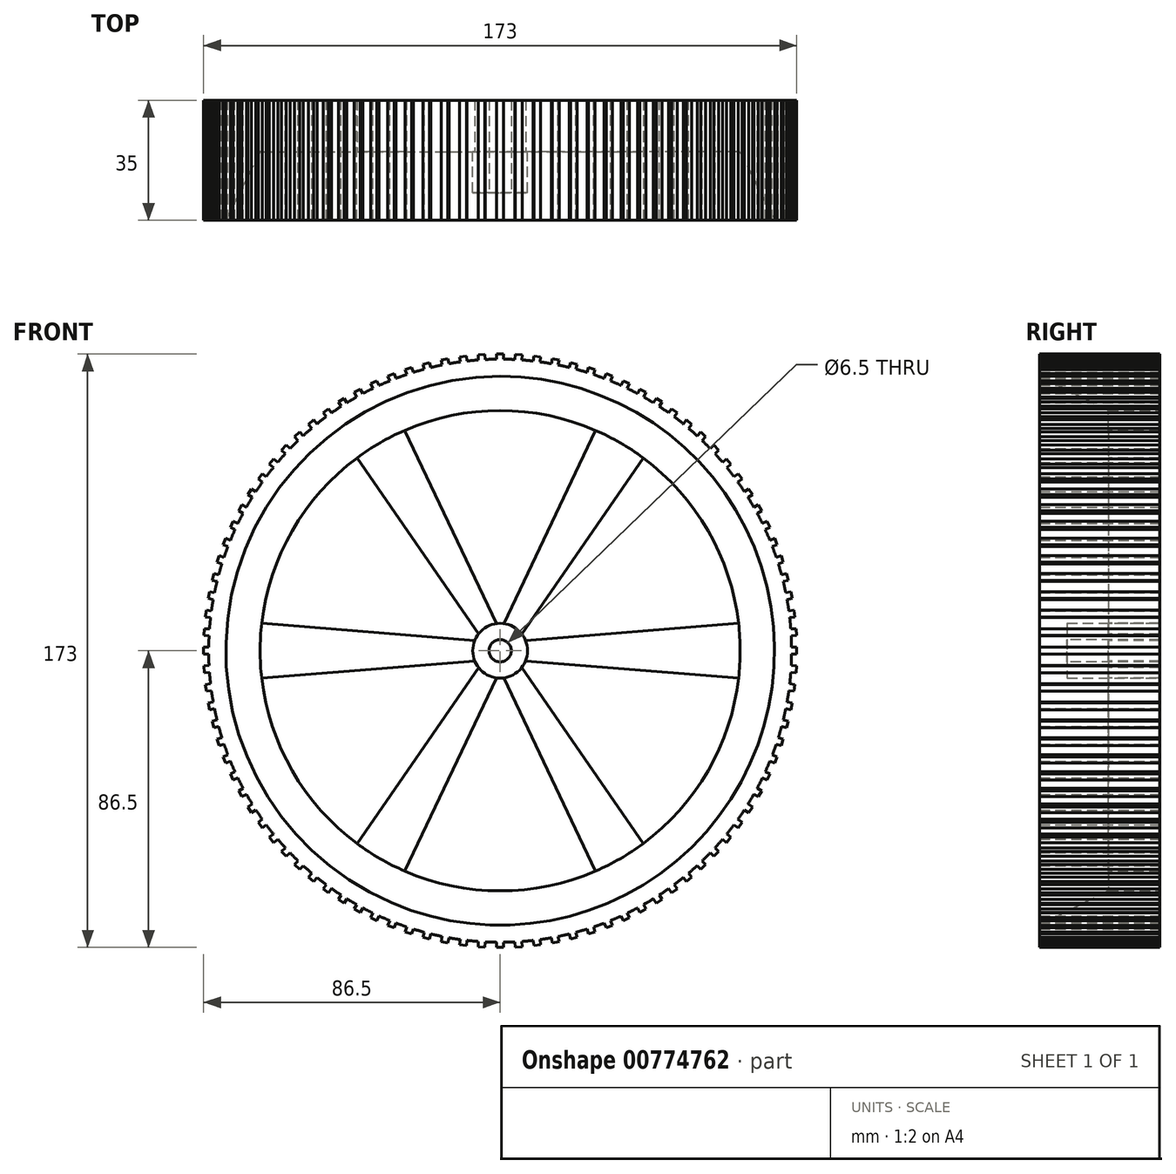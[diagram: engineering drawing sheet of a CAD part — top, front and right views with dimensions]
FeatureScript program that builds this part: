
annotation { "Feature Type Name" : "Feature", "Feature Type Description" : "" }
export const myFeature = defineFeature(function(context is Context, id is Id, definition is map)
    precondition{}
    {
        {
            var Q0;
            Q0=qCreatedBy(makeId("Top.planeOp"),FACE);
            var sketch = newSketch(context, id + "F0", { "sketchPlane" : qUnion([Q0])});
            skLineSegment(sketch, "E0.MirrorCS", {"start": v(-85, -20) * mm, "end": v(-80, -20) * mm});
            skLineSegment(sketch, "E1", {"start": v(-85, 15) * mm, "end": v(0, 15) * mm});
            skLineSegment(sketch, "E2", {"start": v(0, 15) * mm, "end": v(0, 0) * mm});
            skLineSegment(sketch, "E3", {"start": v(-8, 0) * mm, "end": v(-70, 0) * mm});
            skLineSegment(sketch, "E4", {"start": v(-80, -20) * mm, "end": v(-70, 0) * mm});
            skLineSegment(sketch, "E5", {"start": v(-70, 0) * mm, "end": v(-70, 15) * mm});
            skLineSegment(sketch, "E6", {"start": v(-8, 15) * mm, "end": v(-8, 0) * mm});
            skLineSegment(sketch, "E7", {"start": v(-85, 15) * mm, "end": v(-85, -20) * mm});
            skLineSegment(sketch, "E8", {"start": v(0, 0) * mm, "end": v(0, -12) * mm});
            skLineSegment(sketch, "E9", {"start": v(0, -12) * mm, "end": v(-8, -12) * mm});
            skLineSegment(sketch, "E10", {"start": v(-8, -12) * mm, "end": v(-8, 0) * mm});
            skSolve(sketch);
        }
        {
            var Q0;
            Q0=makeQuery(id+"F0.imprint","IMPRINT",FACE,{"disambiguationData":[TD([[makeQuery(id+"F0.imprint","IMPRINT",EDGE,{"derivedFrom":sQuery(id+"F0.wireOp",EDGE,"E0.MirrorCS")}),1.0]])]});
            var Q1;
            {var subQ0=sQuery(id+"F0.wireOp",EDGE,"E2");Q1=makeQuery(id+"F0.imprint","IMPRINT",FACE,{"disambiguationData":[TD([[makeQuery(id+"F0.imprint","IMPRINT",EDGE,{"derivedFrom":subQ0}),-1.0]])]});}
            var Q2;
            Q2=sQuery(id+"F0.wireOp",EDGE,"E2");
            revolve(context, id + "F1", {"surfaceOperationType" : NewSurfaceOperationType.NEW, "entities" : qUnion([Q0, Q1]), "axis" : qUnion([Q2]), "revolveType" : RevolveType.FULL});
        }
        {
            var Q0;
            Q0=qCreatedBy(makeId("Front.planeOp"),FACE);
            var sketch = newSketch(context, id + "F2", { "sketchPlane" : qUnion([Q0])});
            skPoint(sketch, "E11.center", {"position": v(0, 0) * mm});
            skCircle(sketch, "E12.0", {"center": v(0, 0) * mm, "radius": 70 * mm});
            skCircle(sketch, "E13.0", {"center": v(0, 0) * mm, "radius": 8 * mm});
            skLineSegment(sketch, "E14", {"start": v(-69.54, 8) * mm, "end": v(-7.42, 3) * mm});
            skLineSegment(sketch, "E15.MirrorCS", {"start": v(-69.54, -8) * mm, "end": v(-7.42, -3) * mm});
            skLineSegment(sketch, "E16.1.0", {"start": v(-41.7, -56.22) * mm, "end": v(-6.3, -4.92) * mm});
            skLineSegment(sketch, "E16.1.1", {"start": v(-27.84, -64.22) * mm, "end": v(-1.11, -7.92) * mm});
            skLineSegment(sketch, "E16.2.0", {"start": v(27.84, -64.22) * mm, "end": v(1.11, -7.92) * mm});
            skLineSegment(sketch, "E16.2.1", {"start": v(41.7, -56.22) * mm, "end": v(6.3, -4.92) * mm});
            skLineSegment(sketch, "E16.3.0", {"start": v(69.54, -8) * mm, "end": v(7.42, -3) * mm});
            skLineSegment(sketch, "E16.3.1", {"start": v(69.54, 8) * mm, "end": v(7.42, 3) * mm});
            skLineSegment(sketch, "E16.4.0", {"start": v(41.7, 56.22) * mm, "end": v(6.3, 4.92) * mm});
            skLineSegment(sketch, "E16.4.1", {"start": v(27.84, 64.22) * mm, "end": v(1.11, 7.92) * mm});
            skLineSegment(sketch, "E16.5.0", {"start": v(-27.84, 64.22) * mm, "end": v(-1.11, 7.92) * mm});
            skLineSegment(sketch, "E16.5.1", {"start": v(-41.7, 56.22) * mm, "end": v(-6.3, 4.92) * mm});
            skCircle(sketch, "E17.0", {"center": v(0, 0) * mm, "radius": 85 * mm});
            skLineSegment(sketch, "E18", {"start": v(-85, 0) * mm, "end": v(-86.5, 0) * mm, "construction": true});
            skLineSegment(sketch, "E19", {"start": v(-86.5, 1) * mm, "end": v(-86.5, -1) * mm});
            skLineSegment(sketch, "E20", {"start": v(-86.5, 1) * mm, "end": v(-85, 1) * mm});
            skLineSegment(sketch, "E21", {"start": v(-86.5, -1) * mm, "end": v(-85, -1) * mm});
            skLineSegment(sketch, "E22.1.0", {"start": v(-86.27, -6.43) * mm, "end": v(-84.76, -6.33) * mm});
            skLineSegment(sketch, "E22.1.1", {"start": v(-86.4, -4.43) * mm, "end": v(-86.27, -6.43) * mm});
            skLineSegment(sketch, "E22.1.2", {"start": v(-86.4, -4.43) * mm, "end": v(-84.89, -4.34) * mm});
            skLineSegment(sketch, "E22.2.0", {"start": v(-85.7, -11.83) * mm, "end": v(-84.2, -11.64) * mm});
            skLineSegment(sketch, "E22.2.1", {"start": v(-85.94, -9.85) * mm, "end": v(-85.7, -11.83) * mm});
            skLineSegment(sketch, "E22.2.2", {"start": v(-85.94, -9.85) * mm, "end": v(-84.45, -9.66) * mm});
            skLineSegment(sketch, "E22.3.0", {"start": v(-84.78, -17.2) * mm, "end": v(-83.3, -16.9) * mm});
            skLineSegment(sketch, "E22.3.1", {"start": v(-85.16, -15.23) * mm, "end": v(-84.78, -17.2) * mm});
            skLineSegment(sketch, "E22.3.2", {"start": v(-85.16, -15.23) * mm, "end": v(-83.68, -14.94) * mm});
            skLineSegment(sketch, "E22.4.0", {"start": v(-83.53, -22.48) * mm, "end": v(-82.08, -22.1) * mm});
            skLineSegment(sketch, "E22.4.1", {"start": v(-84.03, -20.54) * mm, "end": v(-83.53, -22.48) * mm});
            skLineSegment(sketch, "E22.4.2", {"start": v(-84.03, -20.54) * mm, "end": v(-82.57, -20.17) * mm});
            skLineSegment(sketch, "E22.5.0", {"start": v(-81.96, -27.68) * mm, "end": v(-80.53, -27.22) * mm});
            skLineSegment(sketch, "E22.5.1", {"start": v(-82.58, -25.78) * mm, "end": v(-81.96, -27.68) * mm});
            skLineSegment(sketch, "E22.5.2", {"start": v(-82.58, -25.78) * mm, "end": v(-81.14, -25.31) * mm});
            skLineSegment(sketch, "E22.6.0", {"start": v(-80.06, -32.77) * mm, "end": v(-78.66, -32.22) * mm});
            skLineSegment(sketch, "E22.6.1", {"start": v(-80.8, -30.91) * mm, "end": v(-80.06, -32.77) * mm});
            skLineSegment(sketch, "E22.6.2", {"start": v(-80.8, -30.91) * mm, "end": v(-79.4, -30.36) * mm});
            skLineSegment(sketch, "E22.7.0", {"start": v(-77.84, -37.73) * mm, "end": v(-76.48, -37.1) * mm});
            skLineSegment(sketch, "E22.7.1", {"start": v(-78.7, -35.93) * mm, "end": v(-77.84, -37.73) * mm});
            skLineSegment(sketch, "E22.7.2", {"start": v(-78.7, -35.93) * mm, "end": v(-77.33, -35.28) * mm});
            skLineSegment(sketch, "E22.8.0", {"start": v(-75.32, -42.55) * mm, "end": v(-74, -41.82) * mm});
            skLineSegment(sketch, "E22.8.1", {"start": v(-76.28, -40.8) * mm, "end": v(-75.32, -42.55) * mm});
            skLineSegment(sketch, "E22.8.2", {"start": v(-76.28, -40.8) * mm, "end": v(-74.96, -40.07) * mm});
            skLineSegment(sketch, "E22.9.0", {"start": v(-72.5, -47.2) * mm, "end": v(-71.23, -46.39) * mm});
            skLineSegment(sketch, "E22.9.1", {"start": v(-73.57, -45.5) * mm, "end": v(-72.5, -47.2) * mm});
            skLineSegment(sketch, "E22.9.2", {"start": v(-73.57, -45.5) * mm, "end": v(-72.3, -44.7) * mm});
            skLineSegment(sketch, "E22.10.0", {"start": v(-69.4, -51.65) * mm, "end": v(-68.17, -50.77) * mm});
            skLineSegment(sketch, "E22.10.1", {"start": v(-70.57, -50.03) * mm, "end": v(-69.4, -51.65) * mm});
            skLineSegment(sketch, "E22.10.2", {"start": v(-70.57, -50.03) * mm, "end": v(-69.35, -49.15) * mm});
            skLineSegment(sketch, "E22.11.0", {"start": v(-66.01, -55.9) * mm, "end": v(-64.85, -54.95) * mm});
            skLineSegment(sketch, "E22.11.1", {"start": v(-67.29, -54.37) * mm, "end": v(-66.01, -55.9) * mm});
            skLineSegment(sketch, "E22.11.2", {"start": v(-67.29, -54.37) * mm, "end": v(-66.13, -53.4) * mm});
            skLineSegment(sketch, "E22.12.0", {"start": v(-62.37, -59.94) * mm, "end": v(-61.27, -58.91) * mm});
            skLineSegment(sketch, "E22.12.1", {"start": v(-63.74, -58.48) * mm, "end": v(-62.37, -59.94) * mm});
            skLineSegment(sketch, "E22.12.2", {"start": v(-63.74, -58.48) * mm, "end": v(-62.64, -57.45) * mm});
            skLineSegment(sketch, "E22.13.0", {"start": v(-58.48, -63.74) * mm, "end": v(-57.45, -62.64) * mm});
            skLineSegment(sketch, "E22.13.1", {"start": v(-59.94, -62.37) * mm, "end": v(-58.48, -63.74) * mm});
            skLineSegment(sketch, "E22.13.2", {"start": v(-59.94, -62.37) * mm, "end": v(-58.91, -61.27) * mm});
            skLineSegment(sketch, "E22.14.0", {"start": v(-54.37, -67.29) * mm, "end": v(-53.4, -66.13) * mm});
            skLineSegment(sketch, "E22.14.1", {"start": v(-55.9, -66.01) * mm, "end": v(-54.37, -67.29) * mm});
            skLineSegment(sketch, "E22.14.2", {"start": v(-55.9, -66.01) * mm, "end": v(-54.95, -64.85) * mm});
            skLineSegment(sketch, "E22.15.0", {"start": v(-50.03, -70.57) * mm, "end": v(-49.15, -69.35) * mm});
            skLineSegment(sketch, "E22.15.1", {"start": v(-51.65, -69.4) * mm, "end": v(-50.03, -70.57) * mm});
            skLineSegment(sketch, "E22.15.2", {"start": v(-51.65, -69.4) * mm, "end": v(-50.77, -68.17) * mm});
            skLineSegment(sketch, "E22.16.0", {"start": v(-45.5, -73.57) * mm, "end": v(-44.7, -72.3) * mm});
            skLineSegment(sketch, "E22.16.1", {"start": v(-47.2, -72.5) * mm, "end": v(-45.5, -73.57) * mm});
            skLineSegment(sketch, "E22.16.2", {"start": v(-47.2, -72.5) * mm, "end": v(-46.39, -71.23) * mm});
            skLineSegment(sketch, "E22.17.0", {"start": v(-40.8, -76.28) * mm, "end": v(-40.07, -74.96) * mm});
            skLineSegment(sketch, "E22.17.1", {"start": v(-42.55, -75.32) * mm, "end": v(-40.8, -76.28) * mm});
            skLineSegment(sketch, "E22.17.2", {"start": v(-42.55, -75.32) * mm, "end": v(-41.82, -74) * mm});
            skLineSegment(sketch, "E22.18.0", {"start": v(-35.93, -78.7) * mm, "end": v(-35.28, -77.33) * mm});
            skLineSegment(sketch, "E22.18.1", {"start": v(-37.73, -77.84) * mm, "end": v(-35.93, -78.7) * mm});
            skLineSegment(sketch, "E22.18.2", {"start": v(-37.73, -77.84) * mm, "end": v(-37.1, -76.48) * mm});
            skLineSegment(sketch, "E22.19.0", {"start": v(-30.91, -80.8) * mm, "end": v(-30.36, -79.4) * mm});
            skLineSegment(sketch, "E22.19.1", {"start": v(-32.77, -80.06) * mm, "end": v(-30.91, -80.8) * mm});
            skLineSegment(sketch, "E22.19.2", {"start": v(-32.77, -80.06) * mm, "end": v(-32.22, -78.66) * mm});
            skLineSegment(sketch, "E22.20.0", {"start": v(-25.78, -82.58) * mm, "end": v(-25.31, -81.14) * mm});
            skLineSegment(sketch, "E22.20.1", {"start": v(-27.68, -81.96) * mm, "end": v(-25.78, -82.58) * mm});
            skLineSegment(sketch, "E22.20.2", {"start": v(-27.68, -81.96) * mm, "end": v(-27.22, -80.53) * mm});
            skLineSegment(sketch, "E22.21.0", {"start": v(-20.54, -84.03) * mm, "end": v(-20.17, -82.57) * mm});
            skLineSegment(sketch, "E22.21.1", {"start": v(-22.48, -83.53) * mm, "end": v(-20.54, -84.03) * mm});
            skLineSegment(sketch, "E22.21.2", {"start": v(-22.48, -83.53) * mm, "end": v(-22.1, -82.08) * mm});
            skLineSegment(sketch, "E22.22.0", {"start": v(-15.23, -85.16) * mm, "end": v(-14.94, -83.68) * mm});
            skLineSegment(sketch, "E22.22.1", {"start": v(-17.2, -84.78) * mm, "end": v(-15.23, -85.16) * mm});
            skLineSegment(sketch, "E22.22.2", {"start": v(-17.2, -84.78) * mm, "end": v(-16.9, -83.3) * mm});
            skLineSegment(sketch, "E22.23.0", {"start": v(-9.85, -85.94) * mm, "end": v(-9.66, -84.45) * mm});
            skLineSegment(sketch, "E22.23.1", {"start": v(-11.83, -85.7) * mm, "end": v(-9.85, -85.94) * mm});
            skLineSegment(sketch, "E22.23.2", {"start": v(-11.83, -85.7) * mm, "end": v(-11.64, -84.2) * mm});
            skLineSegment(sketch, "E22.24.0", {"start": v(-4.43, -86.4) * mm, "end": v(-4.34, -84.89) * mm});
            skLineSegment(sketch, "E22.24.1", {"start": v(-6.43, -86.27) * mm, "end": v(-4.43, -86.4) * mm});
            skLineSegment(sketch, "E22.24.2", {"start": v(-6.43, -86.27) * mm, "end": v(-6.33, -84.76) * mm});
            skLineSegment(sketch, "E22.25.0", {"start": v(1, -86.5) * mm, "end": v(1, -85) * mm});
            skLineSegment(sketch, "E22.25.1", {"start": v(-1, -86.5) * mm, "end": v(1, -86.5) * mm});
            skLineSegment(sketch, "E22.25.2", {"start": v(-1, -86.5) * mm, "end": v(-1, -85) * mm});
            skLineSegment(sketch, "E22.26.0", {"start": v(6.43, -86.27) * mm, "end": v(6.33, -84.76) * mm});
            skLineSegment(sketch, "E22.26.1", {"start": v(4.43, -86.4) * mm, "end": v(6.43, -86.27) * mm});
            skLineSegment(sketch, "E22.26.2", {"start": v(4.43, -86.4) * mm, "end": v(4.34, -84.89) * mm});
            skLineSegment(sketch, "E22.27.0", {"start": v(11.83, -85.7) * mm, "end": v(11.64, -84.2) * mm});
            skLineSegment(sketch, "E22.27.1", {"start": v(9.85, -85.94) * mm, "end": v(11.83, -85.7) * mm});
            skLineSegment(sketch, "E22.27.2", {"start": v(9.85, -85.94) * mm, "end": v(9.66, -84.45) * mm});
            skLineSegment(sketch, "E22.28.0", {"start": v(17.2, -84.78) * mm, "end": v(16.9, -83.3) * mm});
            skLineSegment(sketch, "E22.28.1", {"start": v(15.23, -85.16) * mm, "end": v(17.2, -84.78) * mm});
            skLineSegment(sketch, "E22.28.2", {"start": v(15.23, -85.16) * mm, "end": v(14.94, -83.68) * mm});
            skLineSegment(sketch, "E22.29.0", {"start": v(22.48, -83.53) * mm, "end": v(22.1, -82.08) * mm});
            skLineSegment(sketch, "E22.29.1", {"start": v(20.54, -84.03) * mm, "end": v(22.48, -83.53) * mm});
            skLineSegment(sketch, "E22.29.2", {"start": v(20.54, -84.03) * mm, "end": v(20.17, -82.57) * mm});
            skLineSegment(sketch, "E22.30.0", {"start": v(27.68, -81.96) * mm, "end": v(27.22, -80.53) * mm});
            skLineSegment(sketch, "E22.30.1", {"start": v(25.78, -82.58) * mm, "end": v(27.68, -81.96) * mm});
            skLineSegment(sketch, "E22.30.2", {"start": v(25.78, -82.58) * mm, "end": v(25.31, -81.14) * mm});
            skLineSegment(sketch, "E22.31.0", {"start": v(32.77, -80.06) * mm, "end": v(32.22, -78.66) * mm});
            skLineSegment(sketch, "E22.31.1", {"start": v(30.91, -80.8) * mm, "end": v(32.77, -80.06) * mm});
            skLineSegment(sketch, "E22.31.2", {"start": v(30.91, -80.8) * mm, "end": v(30.36, -79.4) * mm});
            skLineSegment(sketch, "E22.32.0", {"start": v(37.73, -77.84) * mm, "end": v(37.1, -76.48) * mm});
            skLineSegment(sketch, "E22.32.1", {"start": v(35.93, -78.7) * mm, "end": v(37.73, -77.84) * mm});
            skLineSegment(sketch, "E22.32.2", {"start": v(35.93, -78.7) * mm, "end": v(35.28, -77.33) * mm});
            skLineSegment(sketch, "E22.33.0", {"start": v(42.55, -75.32) * mm, "end": v(41.82, -74) * mm});
            skLineSegment(sketch, "E22.33.1", {"start": v(40.8, -76.28) * mm, "end": v(42.55, -75.32) * mm});
            skLineSegment(sketch, "E22.33.2", {"start": v(40.8, -76.28) * mm, "end": v(40.07, -74.96) * mm});
            skLineSegment(sketch, "E22.34.0", {"start": v(47.2, -72.5) * mm, "end": v(46.39, -71.23) * mm});
            skLineSegment(sketch, "E22.34.1", {"start": v(45.5, -73.57) * mm, "end": v(47.2, -72.5) * mm});
            skLineSegment(sketch, "E22.34.2", {"start": v(45.5, -73.57) * mm, "end": v(44.7, -72.3) * mm});
            skLineSegment(sketch, "E22.35.0", {"start": v(51.65, -69.4) * mm, "end": v(50.77, -68.17) * mm});
            skLineSegment(sketch, "E22.35.1", {"start": v(50.03, -70.57) * mm, "end": v(51.65, -69.4) * mm});
            skLineSegment(sketch, "E22.35.2", {"start": v(50.03, -70.57) * mm, "end": v(49.15, -69.35) * mm});
            skLineSegment(sketch, "E22.36.0", {"start": v(55.9, -66.01) * mm, "end": v(54.95, -64.85) * mm});
            skLineSegment(sketch, "E22.36.1", {"start": v(54.37, -67.29) * mm, "end": v(55.9, -66.01) * mm});
            skLineSegment(sketch, "E22.36.2", {"start": v(54.37, -67.29) * mm, "end": v(53.4, -66.13) * mm});
            skLineSegment(sketch, "E22.37.0", {"start": v(59.94, -62.37) * mm, "end": v(58.91, -61.27) * mm});
            skLineSegment(sketch, "E22.37.1", {"start": v(58.48, -63.74) * mm, "end": v(59.94, -62.37) * mm});
            skLineSegment(sketch, "E22.37.2", {"start": v(58.48, -63.74) * mm, "end": v(57.45, -62.64) * mm});
            skLineSegment(sketch, "E22.38.0", {"start": v(63.74, -58.48) * mm, "end": v(62.64, -57.45) * mm});
            skLineSegment(sketch, "E22.38.1", {"start": v(62.37, -59.94) * mm, "end": v(63.74, -58.48) * mm});
            skLineSegment(sketch, "E22.38.2", {"start": v(62.37, -59.94) * mm, "end": v(61.27, -58.91) * mm});
            skLineSegment(sketch, "E22.39.0", {"start": v(67.29, -54.37) * mm, "end": v(66.13, -53.4) * mm});
            skLineSegment(sketch, "E22.39.1", {"start": v(66.01, -55.9) * mm, "end": v(67.29, -54.37) * mm});
            skLineSegment(sketch, "E22.39.2", {"start": v(66.01, -55.9) * mm, "end": v(64.85, -54.95) * mm});
            skLineSegment(sketch, "E22.40.0", {"start": v(70.57, -50.03) * mm, "end": v(69.35, -49.15) * mm});
            skLineSegment(sketch, "E22.40.1", {"start": v(69.4, -51.65) * mm, "end": v(70.57, -50.03) * mm});
            skLineSegment(sketch, "E22.40.2", {"start": v(69.4, -51.65) * mm, "end": v(68.17, -50.77) * mm});
            skLineSegment(sketch, "E22.41.0", {"start": v(73.57, -45.5) * mm, "end": v(72.3, -44.7) * mm});
            skLineSegment(sketch, "E22.41.1", {"start": v(72.5, -47.2) * mm, "end": v(73.57, -45.5) * mm});
            skLineSegment(sketch, "E22.41.2", {"start": v(72.5, -47.2) * mm, "end": v(71.23, -46.39) * mm});
            skLineSegment(sketch, "E22.42.0", {"start": v(76.28, -40.8) * mm, "end": v(74.96, -40.07) * mm});
            skLineSegment(sketch, "E22.42.1", {"start": v(75.32, -42.55) * mm, "end": v(76.28, -40.8) * mm});
            skLineSegment(sketch, "E22.42.2", {"start": v(75.32, -42.55) * mm, "end": v(74, -41.82) * mm});
            skLineSegment(sketch, "E22.43.0", {"start": v(78.7, -35.93) * mm, "end": v(77.33, -35.28) * mm});
            skLineSegment(sketch, "E22.43.1", {"start": v(77.84, -37.73) * mm, "end": v(78.7, -35.93) * mm});
            skLineSegment(sketch, "E22.43.2", {"start": v(77.84, -37.73) * mm, "end": v(76.48, -37.1) * mm});
            skLineSegment(sketch, "E22.44.0", {"start": v(80.8, -30.91) * mm, "end": v(79.4, -30.36) * mm});
            skLineSegment(sketch, "E22.44.1", {"start": v(80.06, -32.77) * mm, "end": v(80.8, -30.91) * mm});
            skLineSegment(sketch, "E22.44.2", {"start": v(80.06, -32.77) * mm, "end": v(78.66, -32.22) * mm});
            skLineSegment(sketch, "E22.45.0", {"start": v(82.58, -25.78) * mm, "end": v(81.14, -25.31) * mm});
            skLineSegment(sketch, "E22.45.1", {"start": v(81.96, -27.68) * mm, "end": v(82.58, -25.78) * mm});
            skLineSegment(sketch, "E22.45.2", {"start": v(81.96, -27.68) * mm, "end": v(80.53, -27.22) * mm});
            skLineSegment(sketch, "E22.46.0", {"start": v(84.03, -20.54) * mm, "end": v(82.57, -20.17) * mm});
            skLineSegment(sketch, "E22.46.1", {"start": v(83.53, -22.48) * mm, "end": v(84.03, -20.54) * mm});
            skLineSegment(sketch, "E22.46.2", {"start": v(83.53, -22.48) * mm, "end": v(82.08, -22.1) * mm});
            skLineSegment(sketch, "E22.47.0", {"start": v(85.16, -15.23) * mm, "end": v(83.68, -14.94) * mm});
            skLineSegment(sketch, "E22.47.1", {"start": v(84.78, -17.2) * mm, "end": v(85.16, -15.23) * mm});
            skLineSegment(sketch, "E22.47.2", {"start": v(84.78, -17.2) * mm, "end": v(83.3, -16.9) * mm});
            skLineSegment(sketch, "E22.48.0", {"start": v(85.94, -9.85) * mm, "end": v(84.45, -9.66) * mm});
            skLineSegment(sketch, "E22.48.1", {"start": v(85.7, -11.83) * mm, "end": v(85.94, -9.85) * mm});
            skLineSegment(sketch, "E22.48.2", {"start": v(85.7, -11.83) * mm, "end": v(84.2, -11.64) * mm});
            skLineSegment(sketch, "E22.49.0", {"start": v(86.4, -4.43) * mm, "end": v(84.89, -4.34) * mm});
            skLineSegment(sketch, "E22.49.1", {"start": v(86.27, -6.43) * mm, "end": v(86.4, -4.43) * mm});
            skLineSegment(sketch, "E22.49.2", {"start": v(86.27, -6.43) * mm, "end": v(84.76, -6.33) * mm});
            skLineSegment(sketch, "E22.50.0", {"start": v(86.5, 1) * mm, "end": v(85, 1) * mm});
            skLineSegment(sketch, "E22.50.1", {"start": v(86.5, -1) * mm, "end": v(86.5, 1) * mm});
            skLineSegment(sketch, "E22.50.2", {"start": v(86.5, -1) * mm, "end": v(85, -1) * mm});
            skLineSegment(sketch, "E22.51.0", {"start": v(86.27, 6.43) * mm, "end": v(84.76, 6.33) * mm});
            skLineSegment(sketch, "E22.51.1", {"start": v(86.4, 4.43) * mm, "end": v(86.27, 6.43) * mm});
            skLineSegment(sketch, "E22.51.2", {"start": v(86.4, 4.43) * mm, "end": v(84.89, 4.34) * mm});
            skLineSegment(sketch, "E22.52.0", {"start": v(85.7, 11.83) * mm, "end": v(84.2, 11.64) * mm});
            skLineSegment(sketch, "E22.52.1", {"start": v(85.94, 9.85) * mm, "end": v(85.7, 11.83) * mm});
            skLineSegment(sketch, "E22.52.2", {"start": v(85.94, 9.85) * mm, "end": v(84.45, 9.66) * mm});
            skLineSegment(sketch, "E22.53.0", {"start": v(84.78, 17.2) * mm, "end": v(83.3, 16.9) * mm});
            skLineSegment(sketch, "E22.53.1", {"start": v(85.16, 15.23) * mm, "end": v(84.78, 17.2) * mm});
            skLineSegment(sketch, "E22.53.2", {"start": v(85.16, 15.23) * mm, "end": v(83.68, 14.94) * mm});
            skLineSegment(sketch, "E22.54.0", {"start": v(83.53, 22.48) * mm, "end": v(82.08, 22.1) * mm});
            skLineSegment(sketch, "E22.54.1", {"start": v(84.03, 20.54) * mm, "end": v(83.53, 22.48) * mm});
            skLineSegment(sketch, "E22.54.2", {"start": v(84.03, 20.54) * mm, "end": v(82.57, 20.17) * mm});
            skLineSegment(sketch, "E22.55.0", {"start": v(81.96, 27.68) * mm, "end": v(80.53, 27.22) * mm});
            skLineSegment(sketch, "E22.55.1", {"start": v(82.58, 25.78) * mm, "end": v(81.96, 27.68) * mm});
            skLineSegment(sketch, "E22.55.2", {"start": v(82.58, 25.78) * mm, "end": v(81.14, 25.31) * mm});
            skLineSegment(sketch, "E22.56.0", {"start": v(80.06, 32.77) * mm, "end": v(78.66, 32.22) * mm});
            skLineSegment(sketch, "E22.56.1", {"start": v(80.8, 30.91) * mm, "end": v(80.06, 32.77) * mm});
            skLineSegment(sketch, "E22.56.2", {"start": v(80.8, 30.91) * mm, "end": v(79.4, 30.36) * mm});
            skLineSegment(sketch, "E22.57.0", {"start": v(77.84, 37.73) * mm, "end": v(76.48, 37.1) * mm});
            skLineSegment(sketch, "E22.57.1", {"start": v(78.7, 35.93) * mm, "end": v(77.84, 37.73) * mm});
            skLineSegment(sketch, "E22.57.2", {"start": v(78.7, 35.93) * mm, "end": v(77.33, 35.28) * mm});
            skLineSegment(sketch, "E22.58.0", {"start": v(75.32, 42.55) * mm, "end": v(74, 41.82) * mm});
            skLineSegment(sketch, "E22.58.1", {"start": v(76.28, 40.8) * mm, "end": v(75.32, 42.55) * mm});
            skLineSegment(sketch, "E22.58.2", {"start": v(76.28, 40.8) * mm, "end": v(74.96, 40.07) * mm});
            skLineSegment(sketch, "E22.59.0", {"start": v(72.5, 47.2) * mm, "end": v(71.23, 46.39) * mm});
            skLineSegment(sketch, "E22.59.1", {"start": v(73.57, 45.5) * mm, "end": v(72.5, 47.2) * mm});
            skLineSegment(sketch, "E22.59.2", {"start": v(73.57, 45.5) * mm, "end": v(72.3, 44.7) * mm});
            skLineSegment(sketch, "E22.60.0", {"start": v(69.4, 51.65) * mm, "end": v(68.17, 50.77) * mm});
            skLineSegment(sketch, "E22.60.1", {"start": v(70.57, 50.03) * mm, "end": v(69.4, 51.65) * mm});
            skLineSegment(sketch, "E22.60.2", {"start": v(70.57, 50.03) * mm, "end": v(69.35, 49.15) * mm});
            skLineSegment(sketch, "E22.61.0", {"start": v(66.01, 55.9) * mm, "end": v(64.85, 54.95) * mm});
            skLineSegment(sketch, "E22.61.1", {"start": v(67.29, 54.37) * mm, "end": v(66.01, 55.9) * mm});
            skLineSegment(sketch, "E22.61.2", {"start": v(67.29, 54.37) * mm, "end": v(66.13, 53.4) * mm});
            skLineSegment(sketch, "E22.62.0", {"start": v(62.37, 59.94) * mm, "end": v(61.27, 58.91) * mm});
            skLineSegment(sketch, "E22.62.1", {"start": v(63.74, 58.48) * mm, "end": v(62.37, 59.94) * mm});
            skLineSegment(sketch, "E22.62.2", {"start": v(63.74, 58.48) * mm, "end": v(62.64, 57.45) * mm});
            skLineSegment(sketch, "E22.63.0", {"start": v(58.48, 63.74) * mm, "end": v(57.45, 62.64) * mm});
            skLineSegment(sketch, "E22.63.1", {"start": v(59.94, 62.37) * mm, "end": v(58.48, 63.74) * mm});
            skLineSegment(sketch, "E22.63.2", {"start": v(59.94, 62.37) * mm, "end": v(58.91, 61.27) * mm});
            skLineSegment(sketch, "E22.64.0", {"start": v(54.37, 67.29) * mm, "end": v(53.4, 66.13) * mm});
            skLineSegment(sketch, "E22.64.1", {"start": v(55.9, 66.01) * mm, "end": v(54.37, 67.29) * mm});
            skLineSegment(sketch, "E22.64.2", {"start": v(55.9, 66.01) * mm, "end": v(54.95, 64.85) * mm});
            skLineSegment(sketch, "E22.65.0", {"start": v(50.03, 70.57) * mm, "end": v(49.15, 69.35) * mm});
            skLineSegment(sketch, "E22.65.1", {"start": v(51.65, 69.4) * mm, "end": v(50.03, 70.57) * mm});
            skLineSegment(sketch, "E22.65.2", {"start": v(51.65, 69.4) * mm, "end": v(50.77, 68.17) * mm});
            skLineSegment(sketch, "E22.66.0", {"start": v(45.5, 73.57) * mm, "end": v(44.7, 72.3) * mm});
            skLineSegment(sketch, "E22.66.1", {"start": v(47.2, 72.5) * mm, "end": v(45.5, 73.57) * mm});
            skLineSegment(sketch, "E22.66.2", {"start": v(47.2, 72.5) * mm, "end": v(46.39, 71.23) * mm});
            skLineSegment(sketch, "E22.67.0", {"start": v(40.8, 76.28) * mm, "end": v(40.07, 74.96) * mm});
            skLineSegment(sketch, "E22.67.1", {"start": v(42.55, 75.32) * mm, "end": v(40.8, 76.28) * mm});
            skLineSegment(sketch, "E22.67.2", {"start": v(42.55, 75.32) * mm, "end": v(41.82, 74) * mm});
            skLineSegment(sketch, "E22.68.0", {"start": v(35.93, 78.7) * mm, "end": v(35.28, 77.33) * mm});
            skLineSegment(sketch, "E22.68.1", {"start": v(37.73, 77.84) * mm, "end": v(35.93, 78.7) * mm});
            skLineSegment(sketch, "E22.68.2", {"start": v(37.73, 77.84) * mm, "end": v(37.1, 76.48) * mm});
            skLineSegment(sketch, "E22.69.0", {"start": v(30.91, 80.8) * mm, "end": v(30.36, 79.4) * mm});
            skLineSegment(sketch, "E22.69.1", {"start": v(32.77, 80.06) * mm, "end": v(30.91, 80.8) * mm});
            skLineSegment(sketch, "E22.69.2", {"start": v(32.77, 80.06) * mm, "end": v(32.22, 78.66) * mm});
            skLineSegment(sketch, "E22.70.0", {"start": v(25.78, 82.58) * mm, "end": v(25.31, 81.14) * mm});
            skLineSegment(sketch, "E22.70.1", {"start": v(27.68, 81.96) * mm, "end": v(25.78, 82.58) * mm});
            skLineSegment(sketch, "E22.70.2", {"start": v(27.68, 81.96) * mm, "end": v(27.22, 80.53) * mm});
            skLineSegment(sketch, "E22.71.0", {"start": v(20.54, 84.03) * mm, "end": v(20.17, 82.57) * mm});
            skLineSegment(sketch, "E22.71.1", {"start": v(22.48, 83.53) * mm, "end": v(20.54, 84.03) * mm});
            skLineSegment(sketch, "E22.71.2", {"start": v(22.48, 83.53) * mm, "end": v(22.1, 82.08) * mm});
            skLineSegment(sketch, "E22.72.0", {"start": v(15.23, 85.16) * mm, "end": v(14.94, 83.68) * mm});
            skLineSegment(sketch, "E22.72.1", {"start": v(17.2, 84.78) * mm, "end": v(15.23, 85.16) * mm});
            skLineSegment(sketch, "E22.72.2", {"start": v(17.2, 84.78) * mm, "end": v(16.9, 83.3) * mm});
            skLineSegment(sketch, "E22.73.0", {"start": v(9.85, 85.94) * mm, "end": v(9.66, 84.45) * mm});
            skLineSegment(sketch, "E22.73.1", {"start": v(11.83, 85.7) * mm, "end": v(9.85, 85.94) * mm});
            skLineSegment(sketch, "E22.73.2", {"start": v(11.83, 85.7) * mm, "end": v(11.64, 84.2) * mm});
            skLineSegment(sketch, "E22.74.0", {"start": v(4.43, 86.4) * mm, "end": v(4.34, 84.89) * mm});
            skLineSegment(sketch, "E22.74.1", {"start": v(6.43, 86.27) * mm, "end": v(4.43, 86.4) * mm});
            skLineSegment(sketch, "E22.74.2", {"start": v(6.43, 86.27) * mm, "end": v(6.33, 84.76) * mm});
            skLineSegment(sketch, "E22.75.0", {"start": v(-1, 86.5) * mm, "end": v(-1, 85) * mm});
            skLineSegment(sketch, "E22.75.1", {"start": v(1, 86.5) * mm, "end": v(-1, 86.5) * mm});
            skLineSegment(sketch, "E22.75.2", {"start": v(1, 86.5) * mm, "end": v(1, 85) * mm});
            skLineSegment(sketch, "E22.76.0", {"start": v(-6.43, 86.27) * mm, "end": v(-6.33, 84.76) * mm});
            skLineSegment(sketch, "E22.76.1", {"start": v(-4.43, 86.4) * mm, "end": v(-6.43, 86.27) * mm});
            skLineSegment(sketch, "E22.76.2", {"start": v(-4.43, 86.4) * mm, "end": v(-4.34, 84.89) * mm});
            skLineSegment(sketch, "E22.77.0", {"start": v(-11.83, 85.7) * mm, "end": v(-11.64, 84.2) * mm});
            skLineSegment(sketch, "E22.77.1", {"start": v(-9.85, 85.94) * mm, "end": v(-11.83, 85.7) * mm});
            skLineSegment(sketch, "E22.77.2", {"start": v(-9.85, 85.94) * mm, "end": v(-9.66, 84.45) * mm});
            skLineSegment(sketch, "E22.78.0", {"start": v(-17.2, 84.78) * mm, "end": v(-16.9, 83.3) * mm});
            skLineSegment(sketch, "E22.78.1", {"start": v(-15.23, 85.16) * mm, "end": v(-17.2, 84.78) * mm});
            skLineSegment(sketch, "E22.78.2", {"start": v(-15.23, 85.16) * mm, "end": v(-14.94, 83.68) * mm});
            skLineSegment(sketch, "E22.79.0", {"start": v(-22.48, 83.53) * mm, "end": v(-22.1, 82.08) * mm});
            skLineSegment(sketch, "E22.79.1", {"start": v(-20.54, 84.03) * mm, "end": v(-22.48, 83.53) * mm});
            skLineSegment(sketch, "E22.79.2", {"start": v(-20.54, 84.03) * mm, "end": v(-20.17, 82.57) * mm});
            skLineSegment(sketch, "E22.80.0", {"start": v(-27.68, 81.96) * mm, "end": v(-27.22, 80.53) * mm});
            skLineSegment(sketch, "E22.80.1", {"start": v(-25.78, 82.58) * mm, "end": v(-27.68, 81.96) * mm});
            skLineSegment(sketch, "E22.80.2", {"start": v(-25.78, 82.58) * mm, "end": v(-25.31, 81.14) * mm});
            skLineSegment(sketch, "E22.81.0", {"start": v(-32.77, 80.06) * mm, "end": v(-32.22, 78.66) * mm});
            skLineSegment(sketch, "E22.81.1", {"start": v(-30.91, 80.8) * mm, "end": v(-32.77, 80.06) * mm});
            skLineSegment(sketch, "E22.81.2", {"start": v(-30.91, 80.8) * mm, "end": v(-30.36, 79.4) * mm});
            skLineSegment(sketch, "E22.82.0", {"start": v(-37.73, 77.84) * mm, "end": v(-37.1, 76.48) * mm});
            skLineSegment(sketch, "E22.82.1", {"start": v(-35.93, 78.7) * mm, "end": v(-37.73, 77.84) * mm});
            skLineSegment(sketch, "E22.82.2", {"start": v(-35.93, 78.7) * mm, "end": v(-35.28, 77.33) * mm});
            skLineSegment(sketch, "E22.83.0", {"start": v(-42.55, 75.32) * mm, "end": v(-41.82, 74) * mm});
            skLineSegment(sketch, "E22.83.1", {"start": v(-40.8, 76.28) * mm, "end": v(-42.55, 75.32) * mm});
            skLineSegment(sketch, "E22.83.2", {"start": v(-40.8, 76.28) * mm, "end": v(-40.07, 74.96) * mm});
            skLineSegment(sketch, "E22.84.0", {"start": v(-47.2, 72.5) * mm, "end": v(-46.39, 71.23) * mm});
            skLineSegment(sketch, "E22.84.1", {"start": v(-45.5, 73.57) * mm, "end": v(-47.2, 72.5) * mm});
            skLineSegment(sketch, "E22.84.2", {"start": v(-45.5, 73.57) * mm, "end": v(-44.7, 72.3) * mm});
            skLineSegment(sketch, "E22.85.0", {"start": v(-51.65, 69.4) * mm, "end": v(-50.77, 68.17) * mm});
            skLineSegment(sketch, "E22.85.1", {"start": v(-50.03, 70.57) * mm, "end": v(-51.65, 69.4) * mm});
            skLineSegment(sketch, "E22.85.2", {"start": v(-50.03, 70.57) * mm, "end": v(-49.15, 69.35) * mm});
            skLineSegment(sketch, "E22.86.0", {"start": v(-55.9, 66.01) * mm, "end": v(-54.95, 64.85) * mm});
            skLineSegment(sketch, "E22.86.1", {"start": v(-54.37, 67.29) * mm, "end": v(-55.9, 66.01) * mm});
            skLineSegment(sketch, "E22.86.2", {"start": v(-54.37, 67.29) * mm, "end": v(-53.4, 66.13) * mm});
            skLineSegment(sketch, "E22.87.0", {"start": v(-59.94, 62.37) * mm, "end": v(-58.91, 61.27) * mm});
            skLineSegment(sketch, "E22.87.1", {"start": v(-58.48, 63.74) * mm, "end": v(-59.94, 62.37) * mm});
            skLineSegment(sketch, "E22.87.2", {"start": v(-58.48, 63.74) * mm, "end": v(-57.45, 62.64) * mm});
            skLineSegment(sketch, "E22.88.0", {"start": v(-63.74, 58.48) * mm, "end": v(-62.64, 57.45) * mm});
            skLineSegment(sketch, "E22.88.1", {"start": v(-62.37, 59.94) * mm, "end": v(-63.74, 58.48) * mm});
            skLineSegment(sketch, "E22.88.2", {"start": v(-62.37, 59.94) * mm, "end": v(-61.27, 58.91) * mm});
            skLineSegment(sketch, "E22.89.0", {"start": v(-67.29, 54.37) * mm, "end": v(-66.13, 53.4) * mm});
            skLineSegment(sketch, "E22.89.1", {"start": v(-66.01, 55.9) * mm, "end": v(-67.29, 54.37) * mm});
            skLineSegment(sketch, "E22.89.2", {"start": v(-66.01, 55.9) * mm, "end": v(-64.85, 54.95) * mm});
            skLineSegment(sketch, "E22.90.0", {"start": v(-70.57, 50.03) * mm, "end": v(-69.35, 49.15) * mm});
            skLineSegment(sketch, "E22.90.1", {"start": v(-69.4, 51.65) * mm, "end": v(-70.57, 50.03) * mm});
            skLineSegment(sketch, "E22.90.2", {"start": v(-69.4, 51.65) * mm, "end": v(-68.17, 50.77) * mm});
            skLineSegment(sketch, "E22.91.0", {"start": v(-73.57, 45.5) * mm, "end": v(-72.3, 44.7) * mm});
            skLineSegment(sketch, "E22.91.1", {"start": v(-72.5, 47.2) * mm, "end": v(-73.57, 45.5) * mm});
            skLineSegment(sketch, "E22.91.2", {"start": v(-72.5, 47.2) * mm, "end": v(-71.23, 46.39) * mm});
            skLineSegment(sketch, "E22.92.0", {"start": v(-76.28, 40.8) * mm, "end": v(-74.96, 40.07) * mm});
            skLineSegment(sketch, "E22.92.1", {"start": v(-75.32, 42.55) * mm, "end": v(-76.28, 40.8) * mm});
            skLineSegment(sketch, "E22.92.2", {"start": v(-75.32, 42.55) * mm, "end": v(-74, 41.82) * mm});
            skLineSegment(sketch, "E22.93.0", {"start": v(-78.7, 35.93) * mm, "end": v(-77.33, 35.28) * mm});
            skLineSegment(sketch, "E22.93.1", {"start": v(-77.84, 37.73) * mm, "end": v(-78.7, 35.93) * mm});
            skLineSegment(sketch, "E22.93.2", {"start": v(-77.84, 37.73) * mm, "end": v(-76.48, 37.1) * mm});
            skLineSegment(sketch, "E22.94.0", {"start": v(-80.8, 30.91) * mm, "end": v(-79.4, 30.36) * mm});
            skLineSegment(sketch, "E22.94.1", {"start": v(-80.06, 32.77) * mm, "end": v(-80.8, 30.91) * mm});
            skLineSegment(sketch, "E22.94.2", {"start": v(-80.06, 32.77) * mm, "end": v(-78.66, 32.22) * mm});
            skLineSegment(sketch, "E22.95.0", {"start": v(-82.58, 25.78) * mm, "end": v(-81.14, 25.31) * mm});
            skLineSegment(sketch, "E22.95.1", {"start": v(-81.96, 27.68) * mm, "end": v(-82.58, 25.78) * mm});
            skLineSegment(sketch, "E22.95.2", {"start": v(-81.96, 27.68) * mm, "end": v(-80.53, 27.22) * mm});
            skLineSegment(sketch, "E22.96.0", {"start": v(-84.03, 20.54) * mm, "end": v(-82.57, 20.17) * mm});
            skLineSegment(sketch, "E22.96.1", {"start": v(-83.53, 22.48) * mm, "end": v(-84.03, 20.54) * mm});
            skLineSegment(sketch, "E22.96.2", {"start": v(-83.53, 22.48) * mm, "end": v(-82.08, 22.1) * mm});
            skLineSegment(sketch, "E22.97.0", {"start": v(-85.16, 15.23) * mm, "end": v(-83.68, 14.94) * mm});
            skLineSegment(sketch, "E22.97.1", {"start": v(-84.78, 17.2) * mm, "end": v(-85.16, 15.23) * mm});
            skLineSegment(sketch, "E22.97.2", {"start": v(-84.78, 17.2) * mm, "end": v(-83.3, 16.9) * mm});
            skLineSegment(sketch, "E22.98.0", {"start": v(-85.94, 9.85) * mm, "end": v(-84.45, 9.66) * mm});
            skLineSegment(sketch, "E22.98.1", {"start": v(-85.7, 11.83) * mm, "end": v(-85.94, 9.85) * mm});
            skLineSegment(sketch, "E22.98.2", {"start": v(-85.7, 11.83) * mm, "end": v(-84.2, 11.64) * mm});
            skLineSegment(sketch, "E22.99.0", {"start": v(-86.4, 4.43) * mm, "end": v(-84.89, 4.34) * mm});
            skLineSegment(sketch, "E22.99.1", {"start": v(-86.27, 6.43) * mm, "end": v(-86.4, 4.43) * mm});
            skLineSegment(sketch, "E22.99.2", {"start": v(-86.27, 6.43) * mm, "end": v(-84.76, 6.33) * mm});
            skSolve(sketch);
        }
        {
            var Q0;
            {var subQ0=sQuery(id+"F2.wireOp",EDGE,"E14");Q0=makeQuery(id+"F2.imprint","IMPRINT",FACE,{"disambiguationData":[TD([[makeQuery(id+"F2.imprint","IMPRINT",EDGE,{"derivedFrom":subQ0}),-1.0]])]});}
            var Q1;
            {var subQ0=sQuery(id+"F2.wireOp",EDGE,"E16.5.0");Q1=makeQuery(id+"F2.imprint","IMPRINT",FACE,{"disambiguationData":[TD([[makeQuery(id+"F2.imprint","IMPRINT",EDGE,{"derivedFrom":subQ0}),-1.0]])]});}
            var Q2;
            {var subQ0=sQuery(id+"F2.wireOp",EDGE,"E16.4.0");Q2=makeQuery(id+"F2.imprint","IMPRINT",FACE,{"disambiguationData":[TD([[makeQuery(id+"F2.imprint","IMPRINT",EDGE,{"derivedFrom":subQ0}),-1.0]])]});}
            var Q3;
            {var subQ0=sQuery(id+"F2.wireOp",EDGE,"E16.3.0");Q3=makeQuery(id+"F2.imprint","IMPRINT",FACE,{"disambiguationData":[TD([[makeQuery(id+"F2.imprint","IMPRINT",EDGE,{"derivedFrom":subQ0}),-1.0]])]});}
            var Q4;
            {var subQ0=sQuery(id+"F2.wireOp",EDGE,"E16.2.0");Q4=makeQuery(id+"F2.imprint","IMPRINT",FACE,{"disambiguationData":[TD([[makeQuery(id+"F2.imprint","IMPRINT",EDGE,{"derivedFrom":subQ0}),-1.0]])]});}
            var Q5;
            {var subQ0=sQuery(id+"F2.wireOp",EDGE,"E16.1.0");Q5=makeQuery(id+"F2.imprint","IMPRINT",FACE,{"disambiguationData":[TD([[makeQuery(id+"F2.imprint","IMPRINT",EDGE,{"derivedFrom":subQ0}),-1.0]])]});}
            extrude(context, id + "F3", {"entities" : qUnion([Q0, Q1, Q2, Q3, Q4, Q5]), "operationType" : NewBodyOperationType.ADD, "oppositeDirection" : true, "depth" : 15 * mm, "offsetDistance" : 25 * mm});
        }
        {
            var Q0;
            {var subQ0=sQuery(id+"F2.wireOp",EDGE,"E22.98.0");Q0=makeQuery(id+"F2.imprint","IMPRINT",FACE,{"disambiguationData":[TD([[makeQuery(id+"F2.imprint","IMPRINT",EDGE,{"derivedFrom":subQ0}),1.0]])]});}
            var Q1;
            {var subQ0=sQuery(id+"F2.wireOp",EDGE,"E22.2.0");Q1=makeQuery(id+"F2.imprint","IMPRINT",FACE,{"disambiguationData":[TD([[makeQuery(id+"F2.imprint","IMPRINT",EDGE,{"derivedFrom":subQ0}),1.0]])]});}
            var Q2;
            {var subQ0=sQuery(id+"F2.wireOp",EDGE,"E22.96.0");Q2=makeQuery(id+"F2.imprint","IMPRINT",FACE,{"disambiguationData":[TD([[makeQuery(id+"F2.imprint","IMPRINT",EDGE,{"derivedFrom":subQ0}),1.0]])]});}
            var Q3;
            {var subQ0=sQuery(id+"F2.wireOp",EDGE,"E22.97.0");Q3=makeQuery(id+"F2.imprint","IMPRINT",FACE,{"disambiguationData":[TD([[makeQuery(id+"F2.imprint","IMPRINT",EDGE,{"derivedFrom":subQ0}),1.0]])]});}
            var Q4;
            {var subQ0=sQuery(id+"F2.wireOp",EDGE,"E22.99.0");Q4=makeQuery(id+"F2.imprint","IMPRINT",FACE,{"disambiguationData":[TD([[makeQuery(id+"F2.imprint","IMPRINT",EDGE,{"derivedFrom":subQ0}),1.0]])]});}
            var Q5;
            {var subQ0=sQuery(id+"F2.wireOp",EDGE,"E22.1.0");Q5=makeQuery(id+"F2.imprint","IMPRINT",FACE,{"disambiguationData":[TD([[makeQuery(id+"F2.imprint","IMPRINT",EDGE,{"derivedFrom":subQ0}),1.0]])]});}
            var Q6;
            {var subQ0=sQuery(id+"F2.wireOp",EDGE,"E22.3.0");Q6=makeQuery(id+"F2.imprint","IMPRINT",FACE,{"disambiguationData":[TD([[makeQuery(id+"F2.imprint","IMPRINT",EDGE,{"derivedFrom":subQ0}),1.0]])]});}
            var Q7;
            {var subQ0=sQuery(id+"F2.wireOp",EDGE,"E22.4.0");Q7=makeQuery(id+"F2.imprint","IMPRINT",FACE,{"disambiguationData":[TD([[makeQuery(id+"F2.imprint","IMPRINT",EDGE,{"derivedFrom":subQ0}),1.0]])]});}
            var Q8;
            {var subQ0=sQuery(id+"F2.wireOp",EDGE,"E22.5.0");Q8=makeQuery(id+"F2.imprint","IMPRINT",FACE,{"disambiguationData":[TD([[makeQuery(id+"F2.imprint","IMPRINT",EDGE,{"derivedFrom":subQ0}),1.0]])]});}
            var Q9;
            {var subQ0=sQuery(id+"F2.wireOp",EDGE,"E22.6.0");Q9=makeQuery(id+"F2.imprint","IMPRINT",FACE,{"disambiguationData":[TD([[makeQuery(id+"F2.imprint","IMPRINT",EDGE,{"derivedFrom":subQ0}),1.0]])]});}
            var Q10;
            {var subQ0=sQuery(id+"F2.wireOp",EDGE,"E22.90.0");Q10=makeQuery(id+"F2.imprint","IMPRINT",FACE,{"disambiguationData":[TD([[makeQuery(id+"F2.imprint","IMPRINT",EDGE,{"derivedFrom":subQ0}),1.0]])]});}
            var Q11;
            {var subQ0=sQuery(id+"F2.wireOp",EDGE,"E22.7.0");Q11=makeQuery(id+"F2.imprint","IMPRINT",FACE,{"disambiguationData":[TD([[makeQuery(id+"F2.imprint","IMPRINT",EDGE,{"derivedFrom":subQ0}),1.0]])]});}
            var Q12;
            {var subQ0=sQuery(id+"F2.wireOp",EDGE,"E22.91.0");Q12=makeQuery(id+"F2.imprint","IMPRINT",FACE,{"disambiguationData":[TD([[makeQuery(id+"F2.imprint","IMPRINT",EDGE,{"derivedFrom":subQ0}),1.0]])]});}
            var Q13;
            {var subQ0=sQuery(id+"F2.wireOp",EDGE,"E22.8.0");Q13=makeQuery(id+"F2.imprint","IMPRINT",FACE,{"disambiguationData":[TD([[makeQuery(id+"F2.imprint","IMPRINT",EDGE,{"derivedFrom":subQ0}),1.0]])]});}
            var Q14;
            {var subQ0=sQuery(id+"F2.wireOp",EDGE,"E22.92.0");Q14=makeQuery(id+"F2.imprint","IMPRINT",FACE,{"disambiguationData":[TD([[makeQuery(id+"F2.imprint","IMPRINT",EDGE,{"derivedFrom":subQ0}),1.0]])]});}
            var Q15;
            {var subQ0=sQuery(id+"F2.wireOp",EDGE,"E22.9.0");Q15=makeQuery(id+"F2.imprint","IMPRINT",FACE,{"disambiguationData":[TD([[makeQuery(id+"F2.imprint","IMPRINT",EDGE,{"derivedFrom":subQ0}),1.0]])]});}
            var Q16;
            {var subQ0=sQuery(id+"F2.wireOp",EDGE,"E22.93.0");Q16=makeQuery(id+"F2.imprint","IMPRINT",FACE,{"disambiguationData":[TD([[makeQuery(id+"F2.imprint","IMPRINT",EDGE,{"derivedFrom":subQ0}),1.0]])]});}
            var Q17;
            {var subQ0=sQuery(id+"F2.wireOp",EDGE,"E22.10.0");Q17=makeQuery(id+"F2.imprint","IMPRINT",FACE,{"disambiguationData":[TD([[makeQuery(id+"F2.imprint","IMPRINT",EDGE,{"derivedFrom":subQ0}),1.0]])]});}
            var Q18;
            {var subQ0=sQuery(id+"F2.wireOp",EDGE,"E22.94.0");Q18=makeQuery(id+"F2.imprint","IMPRINT",FACE,{"disambiguationData":[TD([[makeQuery(id+"F2.imprint","IMPRINT",EDGE,{"derivedFrom":subQ0}),1.0]])]});}
            var Q19;
            {var subQ0=sQuery(id+"F2.wireOp",EDGE,"E22.95.0");Q19=makeQuery(id+"F2.imprint","IMPRINT",FACE,{"disambiguationData":[TD([[makeQuery(id+"F2.imprint","IMPRINT",EDGE,{"derivedFrom":subQ0}),1.0]])]});}
            var Q20;
            Q20=makeQuery(id+"F2.imprint","IMPRINT",FACE,{"disambiguationData":[TD([[makeQuery(id+"F2.imprint","IMPRINT",EDGE,{"derivedFrom":sQuery(id+"F2.wireOp",EDGE,"E19")}),1.0]])]});
            var Q21;
            {var subQ0=sQuery(id+"F2.wireOp",EDGE,"E22.86.0");Q21=makeQuery(id+"F2.imprint","IMPRINT",FACE,{"disambiguationData":[TD([[makeQuery(id+"F2.imprint","IMPRINT",EDGE,{"derivedFrom":subQ0}),1.0]])]});}
            var Q22;
            {var subQ0=sQuery(id+"F2.wireOp",EDGE,"E22.84.0");Q22=makeQuery(id+"F2.imprint","IMPRINT",FACE,{"disambiguationData":[TD([[makeQuery(id+"F2.imprint","IMPRINT",EDGE,{"derivedFrom":subQ0}),1.0]])]});}
            var Q23;
            {var subQ0=sQuery(id+"F2.wireOp",EDGE,"E22.85.0");Q23=makeQuery(id+"F2.imprint","IMPRINT",FACE,{"disambiguationData":[TD([[makeQuery(id+"F2.imprint","IMPRINT",EDGE,{"derivedFrom":subQ0}),1.0]])]});}
            var Q24;
            {var subQ0=sQuery(id+"F2.wireOp",EDGE,"E22.87.0");Q24=makeQuery(id+"F2.imprint","IMPRINT",FACE,{"disambiguationData":[TD([[makeQuery(id+"F2.imprint","IMPRINT",EDGE,{"derivedFrom":subQ0}),1.0]])]});}
            var Q25;
            {var subQ0=sQuery(id+"F2.wireOp",EDGE,"E22.88.0");Q25=makeQuery(id+"F2.imprint","IMPRINT",FACE,{"disambiguationData":[TD([[makeQuery(id+"F2.imprint","IMPRINT",EDGE,{"derivedFrom":subQ0}),1.0]])]});}
            var Q26;
            {var subQ0=sQuery(id+"F2.wireOp",EDGE,"E22.89.0");Q26=makeQuery(id+"F2.imprint","IMPRINT",FACE,{"disambiguationData":[TD([[makeQuery(id+"F2.imprint","IMPRINT",EDGE,{"derivedFrom":subQ0}),1.0]])]});}
            var Q27;
            {var subQ0=sQuery(id+"F2.wireOp",EDGE,"E22.82.0");Q27=makeQuery(id+"F2.imprint","IMPRINT",FACE,{"disambiguationData":[TD([[makeQuery(id+"F2.imprint","IMPRINT",EDGE,{"derivedFrom":subQ0}),1.0]])]});}
            var Q28;
            {var subQ0=sQuery(id+"F2.wireOp",EDGE,"E22.81.0");Q28=makeQuery(id+"F2.imprint","IMPRINT",FACE,{"disambiguationData":[TD([[makeQuery(id+"F2.imprint","IMPRINT",EDGE,{"derivedFrom":subQ0}),1.0]])]});}
            var Q29;
            {var subQ0=sQuery(id+"F2.wireOp",EDGE,"E22.68.0");Q29=makeQuery(id+"F2.imprint","IMPRINT",FACE,{"disambiguationData":[TD([[makeQuery(id+"F2.imprint","IMPRINT",EDGE,{"derivedFrom":subQ0}),1.0]])]});}
            var Q30;
            {var subQ0=sQuery(id+"F2.wireOp",EDGE,"E22.69.0");Q30=makeQuery(id+"F2.imprint","IMPRINT",FACE,{"disambiguationData":[TD([[makeQuery(id+"F2.imprint","IMPRINT",EDGE,{"derivedFrom":subQ0}),1.0]])]});}
            var Q31;
            {var subQ0=sQuery(id+"F2.wireOp",EDGE,"E22.70.0");Q31=makeQuery(id+"F2.imprint","IMPRINT",FACE,{"disambiguationData":[TD([[makeQuery(id+"F2.imprint","IMPRINT",EDGE,{"derivedFrom":subQ0}),1.0]])]});}
            var Q32;
            {var subQ0=sQuery(id+"F2.wireOp",EDGE,"E22.80.0");Q32=makeQuery(id+"F2.imprint","IMPRINT",FACE,{"disambiguationData":[TD([[makeQuery(id+"F2.imprint","IMPRINT",EDGE,{"derivedFrom":subQ0}),1.0]])]});}
            var Q33;
            {var subQ0=sQuery(id+"F2.wireOp",EDGE,"E22.83.0");Q33=makeQuery(id+"F2.imprint","IMPRINT",FACE,{"disambiguationData":[TD([[makeQuery(id+"F2.imprint","IMPRINT",EDGE,{"derivedFrom":subQ0}),1.0]])]});}
            var Q34;
            {var subQ0=sQuery(id+"F2.wireOp",EDGE,"E22.71.0");Q34=makeQuery(id+"F2.imprint","IMPRINT",FACE,{"disambiguationData":[TD([[makeQuery(id+"F2.imprint","IMPRINT",EDGE,{"derivedFrom":subQ0}),1.0]])]});}
            var Q35;
            {var subQ0=sQuery(id+"F2.wireOp",EDGE,"E22.72.0");Q35=makeQuery(id+"F2.imprint","IMPRINT",FACE,{"disambiguationData":[TD([[makeQuery(id+"F2.imprint","IMPRINT",EDGE,{"derivedFrom":subQ0}),1.0]])]});}
            var Q36;
            {var subQ0=sQuery(id+"F2.wireOp",EDGE,"E22.73.0");Q36=makeQuery(id+"F2.imprint","IMPRINT",FACE,{"disambiguationData":[TD([[makeQuery(id+"F2.imprint","IMPRINT",EDGE,{"derivedFrom":subQ0}),1.0]])]});}
            var Q37;
            {var subQ0=sQuery(id+"F2.wireOp",EDGE,"E22.74.0");Q37=makeQuery(id+"F2.imprint","IMPRINT",FACE,{"disambiguationData":[TD([[makeQuery(id+"F2.imprint","IMPRINT",EDGE,{"derivedFrom":subQ0}),1.0]])]});}
            var Q38;
            {var subQ0=sQuery(id+"F2.wireOp",EDGE,"E22.75.0");Q38=makeQuery(id+"F2.imprint","IMPRINT",FACE,{"disambiguationData":[TD([[makeQuery(id+"F2.imprint","IMPRINT",EDGE,{"derivedFrom":subQ0}),1.0]])]});}
            var Q39;
            {var subQ0=sQuery(id+"F2.wireOp",EDGE,"E22.76.0");Q39=makeQuery(id+"F2.imprint","IMPRINT",FACE,{"disambiguationData":[TD([[makeQuery(id+"F2.imprint","IMPRINT",EDGE,{"derivedFrom":subQ0}),1.0]])]});}
            var Q40;
            {var subQ0=sQuery(id+"F2.wireOp",EDGE,"E22.77.0");Q40=makeQuery(id+"F2.imprint","IMPRINT",FACE,{"disambiguationData":[TD([[makeQuery(id+"F2.imprint","IMPRINT",EDGE,{"derivedFrom":subQ0}),1.0]])]});}
            var Q41;
            {var subQ0=sQuery(id+"F2.wireOp",EDGE,"E22.78.0");Q41=makeQuery(id+"F2.imprint","IMPRINT",FACE,{"disambiguationData":[TD([[makeQuery(id+"F2.imprint","IMPRINT",EDGE,{"derivedFrom":subQ0}),1.0]])]});}
            var Q42;
            {var subQ0=sQuery(id+"F2.wireOp",EDGE,"E22.79.0");Q42=makeQuery(id+"F2.imprint","IMPRINT",FACE,{"disambiguationData":[TD([[makeQuery(id+"F2.imprint","IMPRINT",EDGE,{"derivedFrom":subQ0}),1.0]])]});}
            var Q43;
            {var subQ0=sQuery(id+"F2.wireOp",EDGE,"E22.67.0");Q43=makeQuery(id+"F2.imprint","IMPRINT",FACE,{"disambiguationData":[TD([[makeQuery(id+"F2.imprint","IMPRINT",EDGE,{"derivedFrom":subQ0}),1.0]])]});}
            var Q44;
            {var subQ0=sQuery(id+"F2.wireOp",EDGE,"E22.66.0");Q44=makeQuery(id+"F2.imprint","IMPRINT",FACE,{"disambiguationData":[TD([[makeQuery(id+"F2.imprint","IMPRINT",EDGE,{"derivedFrom":subQ0}),1.0]])]});}
            var Q45;
            {var subQ0=sQuery(id+"F2.wireOp",EDGE,"E22.64.0");Q45=makeQuery(id+"F2.imprint","IMPRINT",FACE,{"disambiguationData":[TD([[makeQuery(id+"F2.imprint","IMPRINT",EDGE,{"derivedFrom":subQ0}),1.0]])]});}
            var Q46;
            {var subQ0=sQuery(id+"F2.wireOp",EDGE,"E22.63.0");Q46=makeQuery(id+"F2.imprint","IMPRINT",FACE,{"disambiguationData":[TD([[makeQuery(id+"F2.imprint","IMPRINT",EDGE,{"derivedFrom":subQ0}),1.0]])]});}
            var Q47;
            {var subQ0=sQuery(id+"F2.wireOp",EDGE,"E22.60.0");Q47=makeQuery(id+"F2.imprint","IMPRINT",FACE,{"disambiguationData":[TD([[makeQuery(id+"F2.imprint","IMPRINT",EDGE,{"derivedFrom":subQ0}),1.0]])]});}
            var Q48;
            {var subQ0=sQuery(id+"F2.wireOp",EDGE,"E22.61.0");Q48=makeQuery(id+"F2.imprint","IMPRINT",FACE,{"disambiguationData":[TD([[makeQuery(id+"F2.imprint","IMPRINT",EDGE,{"derivedFrom":subQ0}),1.0]])]});}
            var Q49;
            {var subQ0=sQuery(id+"F2.wireOp",EDGE,"E22.62.0");Q49=makeQuery(id+"F2.imprint","IMPRINT",FACE,{"disambiguationData":[TD([[makeQuery(id+"F2.imprint","IMPRINT",EDGE,{"derivedFrom":subQ0}),1.0]])]});}
            var Q50;
            {var subQ0=sQuery(id+"F2.wireOp",EDGE,"E22.54.0");Q50=makeQuery(id+"F2.imprint","IMPRINT",FACE,{"disambiguationData":[TD([[makeQuery(id+"F2.imprint","IMPRINT",EDGE,{"derivedFrom":subQ0}),1.0]])]});}
            var Q51;
            {var subQ0=sQuery(id+"F2.wireOp",EDGE,"E22.55.0");Q51=makeQuery(id+"F2.imprint","IMPRINT",FACE,{"disambiguationData":[TD([[makeQuery(id+"F2.imprint","IMPRINT",EDGE,{"derivedFrom":subQ0}),1.0]])]});}
            var Q52;
            {var subQ0=sQuery(id+"F2.wireOp",EDGE,"E22.56.0");Q52=makeQuery(id+"F2.imprint","IMPRINT",FACE,{"disambiguationData":[TD([[makeQuery(id+"F2.imprint","IMPRINT",EDGE,{"derivedFrom":subQ0}),1.0]])]});}
            var Q53;
            {var subQ0=sQuery(id+"F2.wireOp",EDGE,"E22.57.0");Q53=makeQuery(id+"F2.imprint","IMPRINT",FACE,{"disambiguationData":[TD([[makeQuery(id+"F2.imprint","IMPRINT",EDGE,{"derivedFrom":subQ0}),1.0]])]});}
            var Q54;
            {var subQ0=sQuery(id+"F2.wireOp",EDGE,"E22.58.0");Q54=makeQuery(id+"F2.imprint","IMPRINT",FACE,{"disambiguationData":[TD([[makeQuery(id+"F2.imprint","IMPRINT",EDGE,{"derivedFrom":subQ0}),1.0]])]});}
            var Q55;
            {var subQ0=sQuery(id+"F2.wireOp",EDGE,"E22.59.0");Q55=makeQuery(id+"F2.imprint","IMPRINT",FACE,{"disambiguationData":[TD([[makeQuery(id+"F2.imprint","IMPRINT",EDGE,{"derivedFrom":subQ0}),1.0]])]});}
            var Q56;
            {var subQ0=sQuery(id+"F2.wireOp",EDGE,"E22.46.0");Q56=makeQuery(id+"F2.imprint","IMPRINT",FACE,{"disambiguationData":[TD([[makeQuery(id+"F2.imprint","IMPRINT",EDGE,{"derivedFrom":subQ0}),1.0]])]});}
            var Q57;
            {var subQ0=sQuery(id+"F2.wireOp",EDGE,"E22.42.0");Q57=makeQuery(id+"F2.imprint","IMPRINT",FACE,{"disambiguationData":[TD([[makeQuery(id+"F2.imprint","IMPRINT",EDGE,{"derivedFrom":subQ0}),1.0]])]});}
            var Q58;
            {var subQ0=sQuery(id+"F2.wireOp",EDGE,"E22.44.0");Q58=makeQuery(id+"F2.imprint","IMPRINT",FACE,{"disambiguationData":[TD([[makeQuery(id+"F2.imprint","IMPRINT",EDGE,{"derivedFrom":subQ0}),1.0]])]});}
            var Q59;
            {var subQ0=sQuery(id+"F2.wireOp",EDGE,"E22.45.0");Q59=makeQuery(id+"F2.imprint","IMPRINT",FACE,{"disambiguationData":[TD([[makeQuery(id+"F2.imprint","IMPRINT",EDGE,{"derivedFrom":subQ0}),1.0]])]});}
            var Q60;
            {var subQ0=sQuery(id+"F2.wireOp",EDGE,"E22.47.0");Q60=makeQuery(id+"F2.imprint","IMPRINT",FACE,{"disambiguationData":[TD([[makeQuery(id+"F2.imprint","IMPRINT",EDGE,{"derivedFrom":subQ0}),1.0]])]});}
            var Q61;
            {var subQ0=sQuery(id+"F2.wireOp",EDGE,"E22.48.0");Q61=makeQuery(id+"F2.imprint","IMPRINT",FACE,{"disambiguationData":[TD([[makeQuery(id+"F2.imprint","IMPRINT",EDGE,{"derivedFrom":subQ0}),1.0]])]});}
            var Q62;
            {var subQ0=sQuery(id+"F2.wireOp",EDGE,"E22.49.0");Q62=makeQuery(id+"F2.imprint","IMPRINT",FACE,{"disambiguationData":[TD([[makeQuery(id+"F2.imprint","IMPRINT",EDGE,{"derivedFrom":subQ0}),1.0]])]});}
            var Q63;
            {var subQ0=sQuery(id+"F2.wireOp",EDGE,"E22.50.0");Q63=makeQuery(id+"F2.imprint","IMPRINT",FACE,{"disambiguationData":[TD([[makeQuery(id+"F2.imprint","IMPRINT",EDGE,{"derivedFrom":subQ0}),1.0]])]});}
            var Q64;
            {var subQ0=sQuery(id+"F2.wireOp",EDGE,"E22.41.0");Q64=makeQuery(id+"F2.imprint","IMPRINT",FACE,{"disambiguationData":[TD([[makeQuery(id+"F2.imprint","IMPRINT",EDGE,{"derivedFrom":subQ0}),1.0]])]});}
            var Q65;
            {var subQ0=sQuery(id+"F2.wireOp",EDGE,"E22.43.0");Q65=makeQuery(id+"F2.imprint","IMPRINT",FACE,{"disambiguationData":[TD([[makeQuery(id+"F2.imprint","IMPRINT",EDGE,{"derivedFrom":subQ0}),1.0]])]});}
            var Q66;
            {var subQ0=sQuery(id+"F2.wireOp",EDGE,"E22.51.0");Q66=makeQuery(id+"F2.imprint","IMPRINT",FACE,{"disambiguationData":[TD([[makeQuery(id+"F2.imprint","IMPRINT",EDGE,{"derivedFrom":subQ0}),1.0]])]});}
            var Q67;
            {var subQ0=sQuery(id+"F2.wireOp",EDGE,"E22.52.0");Q67=makeQuery(id+"F2.imprint","IMPRINT",FACE,{"disambiguationData":[TD([[makeQuery(id+"F2.imprint","IMPRINT",EDGE,{"derivedFrom":subQ0}),1.0]])]});}
            var Q68;
            {var subQ0=sQuery(id+"F2.wireOp",EDGE,"E22.53.0");Q68=makeQuery(id+"F2.imprint","IMPRINT",FACE,{"disambiguationData":[TD([[makeQuery(id+"F2.imprint","IMPRINT",EDGE,{"derivedFrom":subQ0}),1.0]])]});}
            var Q69;
            {var subQ0=sQuery(id+"F2.wireOp",EDGE,"E22.11.0");Q69=makeQuery(id+"F2.imprint","IMPRINT",FACE,{"disambiguationData":[TD([[makeQuery(id+"F2.imprint","IMPRINT",EDGE,{"derivedFrom":subQ0}),1.0]])]});}
            var Q70;
            {var subQ0=sQuery(id+"F2.wireOp",EDGE,"E22.14.0");Q70=makeQuery(id+"F2.imprint","IMPRINT",FACE,{"disambiguationData":[TD([[makeQuery(id+"F2.imprint","IMPRINT",EDGE,{"derivedFrom":subQ0}),1.0]])]});}
            var Q71;
            {var subQ0=sQuery(id+"F2.wireOp",EDGE,"E22.12.0");Q71=makeQuery(id+"F2.imprint","IMPRINT",FACE,{"disambiguationData":[TD([[makeQuery(id+"F2.imprint","IMPRINT",EDGE,{"derivedFrom":subQ0}),1.0]])]});}
            var Q72;
            {var subQ0=sQuery(id+"F2.wireOp",EDGE,"E22.13.0");Q72=makeQuery(id+"F2.imprint","IMPRINT",FACE,{"disambiguationData":[TD([[makeQuery(id+"F2.imprint","IMPRINT",EDGE,{"derivedFrom":subQ0}),1.0]])]});}
            var Q73;
            {var subQ0=sQuery(id+"F2.wireOp",EDGE,"E22.15.0");Q73=makeQuery(id+"F2.imprint","IMPRINT",FACE,{"disambiguationData":[TD([[makeQuery(id+"F2.imprint","IMPRINT",EDGE,{"derivedFrom":subQ0}),1.0]])]});}
            var Q74;
            {var subQ0=sQuery(id+"F2.wireOp",EDGE,"E22.16.0");Q74=makeQuery(id+"F2.imprint","IMPRINT",FACE,{"disambiguationData":[TD([[makeQuery(id+"F2.imprint","IMPRINT",EDGE,{"derivedFrom":subQ0}),1.0]])]});}
            var Q75;
            {var subQ0=sQuery(id+"F2.wireOp",EDGE,"E22.34.0");Q75=makeQuery(id+"F2.imprint","IMPRINT",FACE,{"disambiguationData":[TD([[makeQuery(id+"F2.imprint","IMPRINT",EDGE,{"derivedFrom":subQ0}),1.0]])]});}
            var Q76;
            {var subQ0=sQuery(id+"F2.wireOp",EDGE,"E22.18.0");Q76=makeQuery(id+"F2.imprint","IMPRINT",FACE,{"disambiguationData":[TD([[makeQuery(id+"F2.imprint","IMPRINT",EDGE,{"derivedFrom":subQ0}),1.0]])]});}
            var Q77;
            {var subQ0=sQuery(id+"F2.wireOp",EDGE,"E22.19.0");Q77=makeQuery(id+"F2.imprint","IMPRINT",FACE,{"disambiguationData":[TD([[makeQuery(id+"F2.imprint","IMPRINT",EDGE,{"derivedFrom":subQ0}),1.0]])]});}
            var Q78;
            {var subQ0=sQuery(id+"F2.wireOp",EDGE,"E22.25.0");Q78=makeQuery(id+"F2.imprint","IMPRINT",FACE,{"disambiguationData":[TD([[makeQuery(id+"F2.imprint","IMPRINT",EDGE,{"derivedFrom":subQ0}),1.0]])]});}
            var Q79;
            {var subQ0=sQuery(id+"F2.wireOp",EDGE,"E22.30.0");Q79=makeQuery(id+"F2.imprint","IMPRINT",FACE,{"disambiguationData":[TD([[makeQuery(id+"F2.imprint","IMPRINT",EDGE,{"derivedFrom":subQ0}),1.0]])]});}
            var Q80;
            {var subQ0=sQuery(id+"F2.wireOp",EDGE,"E22.28.0");Q80=makeQuery(id+"F2.imprint","IMPRINT",FACE,{"disambiguationData":[TD([[makeQuery(id+"F2.imprint","IMPRINT",EDGE,{"derivedFrom":subQ0}),1.0]])]});}
            var Q81;
            {var subQ0=sQuery(id+"F2.wireOp",EDGE,"E22.29.0");Q81=makeQuery(id+"F2.imprint","IMPRINT",FACE,{"disambiguationData":[TD([[makeQuery(id+"F2.imprint","IMPRINT",EDGE,{"derivedFrom":subQ0}),1.0]])]});}
            var Q82;
            {var subQ0=sQuery(id+"F2.wireOp",EDGE,"E22.31.0");Q82=makeQuery(id+"F2.imprint","IMPRINT",FACE,{"disambiguationData":[TD([[makeQuery(id+"F2.imprint","IMPRINT",EDGE,{"derivedFrom":subQ0}),1.0]])]});}
            var Q83;
            {var subQ0=sQuery(id+"F2.wireOp",EDGE,"E22.32.0");Q83=makeQuery(id+"F2.imprint","IMPRINT",FACE,{"disambiguationData":[TD([[makeQuery(id+"F2.imprint","IMPRINT",EDGE,{"derivedFrom":subQ0}),1.0]])]});}
            var Q84;
            {var subQ0=sQuery(id+"F2.wireOp",EDGE,"E22.33.0");Q84=makeQuery(id+"F2.imprint","IMPRINT",FACE,{"disambiguationData":[TD([[makeQuery(id+"F2.imprint","IMPRINT",EDGE,{"derivedFrom":subQ0}),1.0]])]});}
            var Q85;
            {var subQ0=sQuery(id+"F2.wireOp",EDGE,"E22.17.0");Q85=makeQuery(id+"F2.imprint","IMPRINT",FACE,{"disambiguationData":[TD([[makeQuery(id+"F2.imprint","IMPRINT",EDGE,{"derivedFrom":subQ0}),1.0]])]});}
            var Q86;
            {var subQ0=sQuery(id+"F2.wireOp",EDGE,"E22.20.0");Q86=makeQuery(id+"F2.imprint","IMPRINT",FACE,{"disambiguationData":[TD([[makeQuery(id+"F2.imprint","IMPRINT",EDGE,{"derivedFrom":subQ0}),1.0]])]});}
            var Q87;
            {var subQ0=sQuery(id+"F2.wireOp",EDGE,"E22.21.0");Q87=makeQuery(id+"F2.imprint","IMPRINT",FACE,{"disambiguationData":[TD([[makeQuery(id+"F2.imprint","IMPRINT",EDGE,{"derivedFrom":subQ0}),1.0]])]});}
            var Q88;
            {var subQ0=sQuery(id+"F2.wireOp",EDGE,"E22.22.0");Q88=makeQuery(id+"F2.imprint","IMPRINT",FACE,{"disambiguationData":[TD([[makeQuery(id+"F2.imprint","IMPRINT",EDGE,{"derivedFrom":subQ0}),1.0]])]});}
            var Q89;
            {var subQ0=sQuery(id+"F2.wireOp",EDGE,"E22.23.0");Q89=makeQuery(id+"F2.imprint","IMPRINT",FACE,{"disambiguationData":[TD([[makeQuery(id+"F2.imprint","IMPRINT",EDGE,{"derivedFrom":subQ0}),1.0]])]});}
            var Q90;
            {var subQ0=sQuery(id+"F2.wireOp",EDGE,"E22.24.0");Q90=makeQuery(id+"F2.imprint","IMPRINT",FACE,{"disambiguationData":[TD([[makeQuery(id+"F2.imprint","IMPRINT",EDGE,{"derivedFrom":subQ0}),1.0]])]});}
            var Q91;
            {var subQ0=sQuery(id+"F2.wireOp",EDGE,"E22.26.0");Q91=makeQuery(id+"F2.imprint","IMPRINT",FACE,{"disambiguationData":[TD([[makeQuery(id+"F2.imprint","IMPRINT",EDGE,{"derivedFrom":subQ0}),1.0]])]});}
            var Q92;
            {var subQ0=sQuery(id+"F2.wireOp",EDGE,"E22.27.0");Q92=makeQuery(id+"F2.imprint","IMPRINT",FACE,{"disambiguationData":[TD([[makeQuery(id+"F2.imprint","IMPRINT",EDGE,{"derivedFrom":subQ0}),1.0]])]});}
            var Q93;
            {var subQ0=sQuery(id+"F2.wireOp",EDGE,"E22.35.0");Q93=makeQuery(id+"F2.imprint","IMPRINT",FACE,{"disambiguationData":[TD([[makeQuery(id+"F2.imprint","IMPRINT",EDGE,{"derivedFrom":subQ0}),1.0]])]});}
            var Q94;
            {var subQ0=sQuery(id+"F2.wireOp",EDGE,"E22.36.0");Q94=makeQuery(id+"F2.imprint","IMPRINT",FACE,{"disambiguationData":[TD([[makeQuery(id+"F2.imprint","IMPRINT",EDGE,{"derivedFrom":subQ0}),1.0]])]});}
            var Q95;
            {var subQ0=sQuery(id+"F2.wireOp",EDGE,"E22.37.0");Q95=makeQuery(id+"F2.imprint","IMPRINT",FACE,{"disambiguationData":[TD([[makeQuery(id+"F2.imprint","IMPRINT",EDGE,{"derivedFrom":subQ0}),1.0]])]});}
            var Q96;
            {var subQ0=sQuery(id+"F2.wireOp",EDGE,"E22.39.0");Q96=makeQuery(id+"F2.imprint","IMPRINT",FACE,{"disambiguationData":[TD([[makeQuery(id+"F2.imprint","IMPRINT",EDGE,{"derivedFrom":subQ0}),1.0]])]});}
            var Q97;
            {var subQ0=sQuery(id+"F2.wireOp",EDGE,"E22.38.0");Q97=makeQuery(id+"F2.imprint","IMPRINT",FACE,{"disambiguationData":[TD([[makeQuery(id+"F2.imprint","IMPRINT",EDGE,{"derivedFrom":subQ0}),1.0]])]});}
            var Q98;
            {var subQ0=sQuery(id+"F2.wireOp",EDGE,"E22.40.0");Q98=makeQuery(id+"F2.imprint","IMPRINT",FACE,{"disambiguationData":[TD([[makeQuery(id+"F2.imprint","IMPRINT",EDGE,{"derivedFrom":subQ0}),1.0]])]});}
            var Q99;
            {var subQ0=sQuery(id+"F2.wireOp",EDGE,"E22.65.0");Q99=makeQuery(id+"F2.imprint","IMPRINT",FACE,{"disambiguationData":[TD([[makeQuery(id+"F2.imprint","IMPRINT",EDGE,{"derivedFrom":subQ0}),1.0]])]});}
            extrude(context, id + "F4", {"entities" : qUnion([Q0, Q1, Q2, Q3, Q4, Q5, Q6, Q7, Q8, Q9, Q10, Q11, Q12, Q13, Q14, Q15, Q16, Q17, Q18, Q19, Q20, Q21, Q22, Q23, Q24, Q25, Q26, Q27, Q28, Q29, Q30, Q31, Q32, Q33, Q34, Q35, Q36, Q37, Q38, Q39, Q40, Q41, Q42, Q43, Q44, Q45, Q46, Q47, Q48, Q49, Q50, Q51, Q52, Q53, Q54, Q55, Q56, Q57, Q58, Q59, Q60, Q61, Q62, Q63, Q64, Q65, Q66, Q67, Q68, Q69, Q70, Q71, Q72, Q73, Q74, Q75, Q76, Q77, Q78, Q79, Q80, Q81, Q82, Q83, Q84, Q85, Q86, Q87, Q88, Q89, Q90, Q91, Q92, Q93, Q94, Q95, Q96, Q97, Q98, Q99]), "operationType" : NewBodyOperationType.ADD, "depth" : 20 * mm, "offsetDistance" : 25 * mm, "hasSecondDirection" : true, "secondDirectionOppositeDirection" : true, "secondDirectionDepth" : 15 * mm});
        }
        {
            var Q0;
            Q0=makeQuery(id+"F1.opRevolve","SWEPT_FACE",FACE,{"disambiguationData":[OSD([sQuery(id+"F0.wireOp",EDGE,"E9")])]});
            var sketch = newSketch(context, id + "F5", { "sketchPlane" : qUnion([Q0])});
            skPoint(sketch, "E23.0", {"position": v(0, 0) * mm});
            skSolve(sketch);
        }
        {
            var Q0;
            Q0=sQuery(id+"F5.wireOp",VERTEX,"E23.0");
            var Q1;
            Q1=makeQuery(id+"F1.opRevolve","SWEPT_BODY",BODY,{"disambiguationData":[OSD([sQuery(id+"F0.wireOp",EDGE,"E0.MirrorCS"),sQuery(id+"F0.wireOp",EDGE,"E1"),sQuery(id+"F0.wireOp",EDGE,"E4"),sQuery(id+"F0.wireOp",EDGE,"E5"),sQuery(id+"F0.wireOp",EDGE,"E7")])]});
            hole(context, id + "F6", {"style" : HoleStyle.SIMPLE, "endStyle" : HoleEndStyle.THROUGH, "holeDiameter" : 6.5 * mm, "majorDiameter" : 5 * mm, "isTappedThrough" : true, "tappedDepth" : 12 * mm, "tapClearance" : 3, "locations" : qUnion([Q0]), "scope" : qUnion([Q1])});
        }
    });
